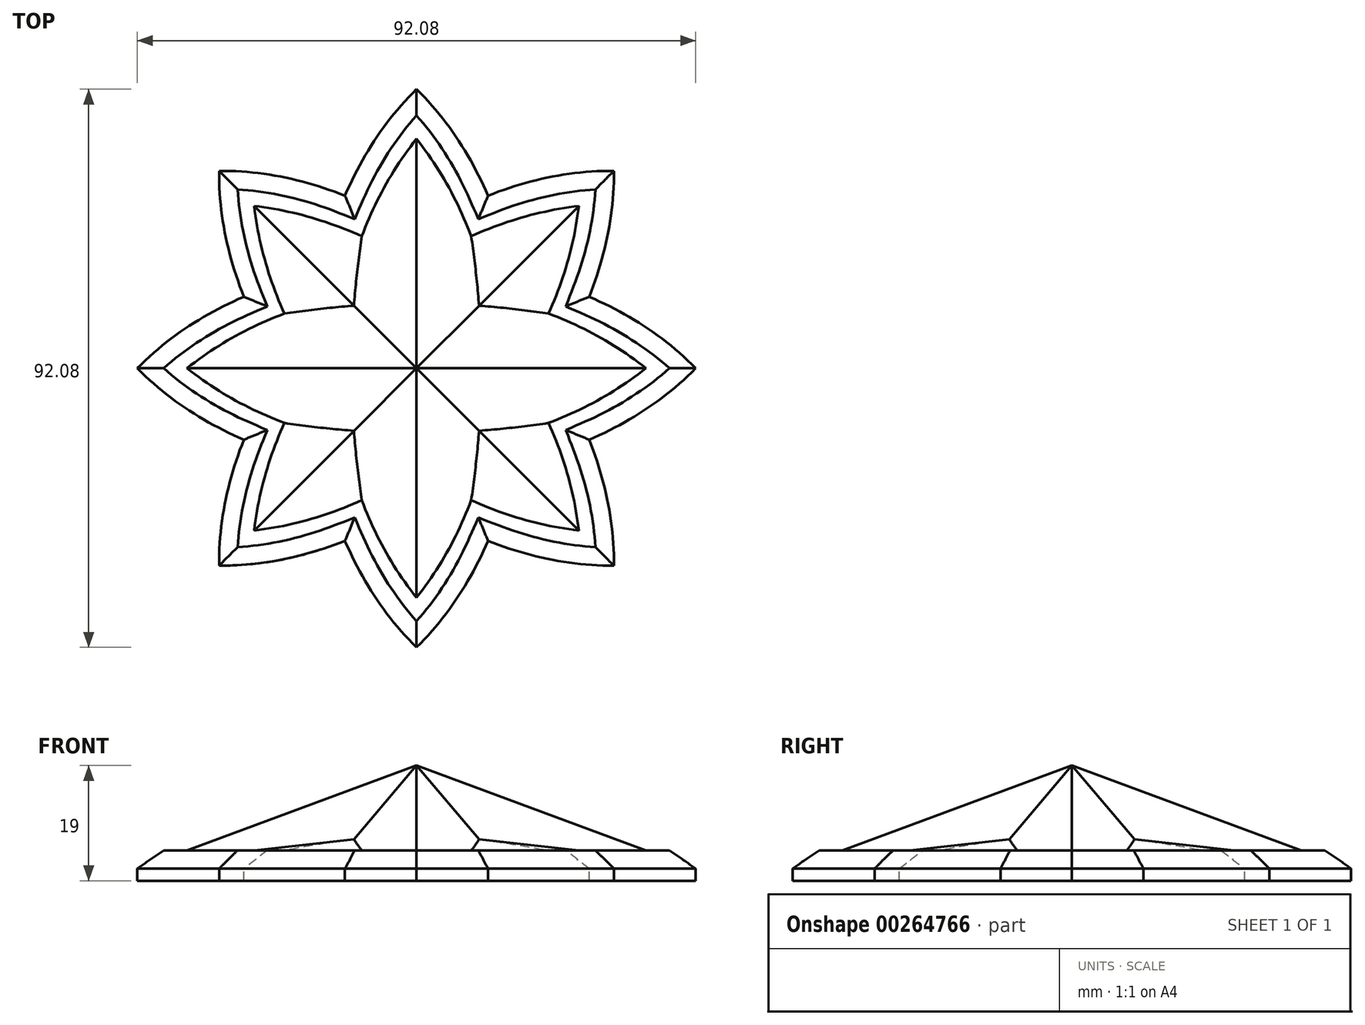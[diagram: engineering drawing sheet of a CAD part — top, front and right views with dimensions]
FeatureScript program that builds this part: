
annotation { "Feature Type Name" : "Feature", "Feature Type Description" : "" }
export const myFeature = defineFeature(function(context is Context, id is Id, definition is map)
    precondition{}
    {
        {
            var Q0;
            Q0=qCreatedBy(makeId("Top.planeOp"),FACE);
            var sketch = newSketch(context, id + "F0", { "sketchPlane" : qUnion([Q0])});
            skLineSegment(sketch, "E0", {"start": v(0, 45.34) * mm, "end": v(0, -44.66) * mm, "construction": true});
            skSolve(sketch);
        }
        {
            var Q0;
            Q0=qCreatedBy(makeId("Top.planeOp"),FACE);
            var sketch = newSketch(context, id + "F1", { "sketchPlane" : qUnion([Q0])});
            skFitSpline(sketch, "E1", {"points": [v(-11.88, 11.88) * mm, v(0, 37.85) * mm], "startDerivative": vector(5.9, 28.28) * mm, "endDerivative": vector(18.18, 22.98) * mm});
            skLineSegment(sketch, "E2", {"start": v(-11.88, 11.88) * mm, "end": v(0, 0) * mm, "construction": true});
            skFitSpline(sketch, "E3.MirrorCS", {"points": [v(11.88, 11.88) * mm, v(0, 37.85) * mm], "startDerivative": vector(-5.9, 28.28) * mm, "endDerivative": vector(-18.18, 22.98) * mm});
            skLineSegment(sketch, "E4.MirrorCS", {"start": v(11.88, 11.88) * mm, "end": v(0, 0) * mm, "construction": true});
            skFitSpline(sketch, "E5.MirrorCS", {"points": [v(-11.88, -11.88) * mm, v(-37.85, 0) * mm], "startDerivative": vector(-28.28, 5.9) * mm, "endDerivative": vector(-22.98, 18.18) * mm});
            skFitSpline(sketch, "E6.MirrorCS", {"points": [v(-11.88, 11.88) * mm, v(-37.85, 0) * mm], "startDerivative": vector(-28.28, -5.9) * mm, "endDerivative": vector(-22.98, -18.18) * mm});
            skFitSpline(sketch, "E7.MirrorCS", {"points": [v(11.88, 11.88) * mm, v(37.85, 0) * mm], "startDerivative": vector(28.28, -5.9) * mm, "endDerivative": vector(22.98, -18.18) * mm});
            skFitSpline(sketch, "E8.MirrorCS", {"points": [v(11.88, -11.88) * mm, v(37.85, 0) * mm], "startDerivative": vector(28.28, 5.9) * mm, "endDerivative": vector(22.98, 18.18) * mm});
            skFitSpline(sketch, "E9.MirrorCS", {"points": [v(11.88, -11.88) * mm, v(0, -37.85) * mm], "startDerivative": vector(-5.9, -28.28) * mm, "endDerivative": vector(-18.18, -22.98) * mm});
            skFitSpline(sketch, "E10.MirrorCS", {"points": [v(-11.88, -11.88) * mm, v(0, -37.85) * mm], "startDerivative": vector(5.9, -28.28) * mm, "endDerivative": vector(18.18, -22.98) * mm});
            skFitSpline(sketch, "E11", {"points": [v(-9.2, 21.3) * mm, v(-26, 26) * mm], "startDerivative": vector(-15.62, 6.86) * mm, "endDerivative": vector(-19.3, 2.67) * mm});
            skLineSegment(sketch, "E12", {"start": v(-26, 26) * mm, "end": v(0, 0) * mm, "construction": true});
            skFitSpline(sketch, "E13.MirrorCS", {"points": [v(9.2, 21.3) * mm, v(26, 26) * mm], "startDerivative": vector(15.62, 6.86) * mm, "endDerivative": vector(19.3, 2.67) * mm});
            skLineSegment(sketch, "E14.MirrorCS", {"start": v(26, 26) * mm, "end": v(0, 0) * mm, "construction": true});
            skFitSpline(sketch, "E15.MirrorCS", {"points": [v(-21.3, 9.2) * mm, v(-26, 26) * mm], "startDerivative": vector(-6.86, 15.62) * mm, "endDerivative": vector(-2.67, 19.3) * mm});
            skFitSpline(sketch, "E16.MirrorCS", {"points": [v(-21.3, -9.2) * mm, v(-26, -26) * mm], "startDerivative": vector(-6.86, -15.62) * mm, "endDerivative": vector(-2.67, -19.3) * mm});
            skFitSpline(sketch, "E17.MirrorCS", {"points": [v(21.3, 9.2) * mm, v(26, 26) * mm], "startDerivative": vector(6.86, 15.62) * mm, "endDerivative": vector(2.67, 19.3) * mm});
            skFitSpline(sketch, "E18.MirrorCS", {"points": [v(21.3, -9.2) * mm, v(26, -26) * mm], "startDerivative": vector(6.86, -15.62) * mm, "endDerivative": vector(2.67, -19.3) * mm});
            skFitSpline(sketch, "E19.MirrorCS", {"points": [v(9.2, -21.3) * mm, v(26, -26) * mm], "startDerivative": vector(15.62, -6.86) * mm, "endDerivative": vector(19.3, -2.67) * mm});
            skFitSpline(sketch, "E20.MirrorCS", {"points": [v(-9.2, -21.3) * mm, v(-26, -26) * mm], "startDerivative": vector(-15.62, -6.86) * mm, "endDerivative": vector(-19.3, -2.67) * mm});
            skSolve(sketch);
        }
        {
            var Q0;
            Q0=qCreatedBy(makeId("Top.planeOp"),FACE);
            cPlane(context, id + "F2", {"entities" : qUnion([Q0]), "cplaneType" : CPlaneType.OFFSET, "offset" : 14 * mm, "width" : 150 * mm, "height" : 150 * mm});
        }
        {
            var Q0;
            Q0=qCreatedBy(id+"F2.planeOp",FACE);
            var sketch = newSketch(context, id + "F3", { "sketchPlane" : qUnion([Q0])});
            skPoint(sketch, "E21", {"position": v(0, 0) * mm});
            skPoint(sketch, "E22", {"position": v(-11.88, -11.88) * mm});
            skPoint(sketch, "E23.MirrorP", {"position": v(11.88, -11.88) * mm});
            skPoint(sketch, "E24.MirrorP", {"position": v(-11.88, 11.88) * mm});
            skPoint(sketch, "E25.MirrorP", {"position": v(11.88, 11.88) * mm});
            skSolve(sketch);
        }
        {
            var Q0;
            {var subQ6=sQuery(id+"F1.wireOp",EDGE,"E6.MirrorCS");var subQ10=sQuery(id+"F1.wireOp",EDGE,"E1");var subQ11=makeQuery(id+"F1.imprint","INTERSECT",VERTEX,{"derivedFrom":[subQ10,subQ6]});Q0=makeQuery(id+"F1.imprint","IMPRINT",FACE,{"disambiguationData":[TD([[makeQuery(id+"F1.imprint","IMPRINT",EDGE,{"disambiguationData":[TD([[subQ11,-1.0]])],"derivedFrom":subQ10}),-1.0]])]});}
            var Q1;
            Q1=sQuery(id+"F3.wireOp",VERTEX,"E21");
            loft(context, id + "F4", {"sheetProfilesArray" : [{ "sheetProfileEntities" : qUnion([Q0]) }, { "sheetProfileEntities" : qUnion([Q1]) }]});
        }
        {
            var Q0;
            Q0=qCreatedBy(makeId("Top.planeOp"),FACE);
            cPlane(context, id + "F5", {"entities" : qUnion([Q0]), "cplaneType" : CPlaneType.OFFSET, "offset" : 3 * mm, "width" : 150 * mm, "height" : 150 * mm});
        }
        {
            var Q0;
            Q0=qCreatedBy(id+"F5.planeOp",FACE);
            var sketch = newSketch(context, id + "F6", { "sketchPlane" : qUnion([Q0])});
            skPoint(sketch, "E26", {"position": v(0, 0) * mm});
            skPoint(sketch, "E27", {"position": v(-11.88, -11.88) * mm});
            skPoint(sketch, "E28.MirrorP", {"position": v(11.88, -11.88) * mm});
            skPoint(sketch, "E29.MirrorP", {"position": v(-11.88, 11.88) * mm});
            skPoint(sketch, "E30.MirrorP", {"position": v(11.88, 11.88) * mm});
            skSolve(sketch);
        }
        {
            var Q0;
            Q0=qCreatedBy(makeId("Top.planeOp"),FACE);
            var sketch = newSketch(context, id + "F7", { "sketchPlane" : qUnion([Q0])});
            skFitSpline(sketch, "E31", {"points": [v(0, 16.8) * mm, v(26.76, 26.76) * mm], "startDerivative": vector(24.17, 15.83) * mm, "endDerivative": vector(29.1, 3.4) * mm});
            skFitSpline(sketch, "E32.MirrorCS", {"points": [v(16.8, 0) * mm, v(26.76, 26.76) * mm], "startDerivative": vector(15.83, 24.17) * mm, "endDerivative": vector(3.4, 29.1) * mm});
            skFitSpline(sketch, "E33.MirrorCS", {"points": [v(-16.8, 0) * mm, v(-26.76, 26.76) * mm], "startDerivative": vector(-15.83, 24.17) * mm, "endDerivative": vector(-3.4, 29.1) * mm});
            skFitSpline(sketch, "E34.MirrorCS", {"points": [v(0, 16.8) * mm, v(-26.76, 26.76) * mm], "startDerivative": vector(-24.17, 15.83) * mm, "endDerivative": vector(-29.1, 3.4) * mm});
            skFitSpline(sketch, "E35.MirrorCS", {"points": [v(16.8, 0) * mm, v(26.76, -26.76) * mm], "startDerivative": vector(15.83, -24.17) * mm, "endDerivative": vector(3.4, -29.1) * mm});
            skFitSpline(sketch, "E36.MirrorCS", {"points": [v(0, -16.8) * mm, v(26.76, -26.76) * mm], "startDerivative": vector(24.17, -15.83) * mm, "endDerivative": vector(29.1, -3.4) * mm});
            skFitSpline(sketch, "E37.MirrorCS", {"points": [v(0, -16.8) * mm, v(-26.76, -26.76) * mm], "startDerivative": vector(-24.17, -15.83) * mm, "endDerivative": vector(-29.1, -3.4) * mm});
            skFitSpline(sketch, "E38.MirrorCS", {"points": [v(-16.8, 0) * mm, v(-26.76, -26.76) * mm], "startDerivative": vector(-15.83, -24.17) * mm, "endDerivative": vector(-3.4, -29.1) * mm});
            skSolve(sketch);
        }
        {
            var Q0;
            Q0=makeQuery(id+"F7.imprint","IMPRINT",FACE,{"disambiguationData":[TD([[makeQuery(id+"F7.imprint","IMPRINT",EDGE,{"derivedFrom":sQuery(id+"F7.wireOp",EDGE,"E31")}),-1.0]])]});
            var Q1;
            Q1=sQuery(id+"F6.wireOp",VERTEX,"E26");
            loft(context, id + "F8", {"operationType" : NewBodyOperationType.ADD, "sheetProfilesArray" : [{ "sheetProfileEntities" : qUnion([Q0]) }, { "sheetProfileEntities" : qUnion([Q1]) }]});
        }
        {
            var Q0;
            Q0=qCreatedBy(makeId("Top.planeOp"),FACE);
            var sketch = newSketch(context, id + "F9", { "sketchPlane" : qUnion([Q0])});
            skFitSpline(sketch, "E39", {"points": [v(-11.8, 28.47) * mm, v(0, 46.04) * mm], "startDerivative": vector(8.54, 19.71) * mm, "endDerivative": vector(15.3, 14.96) * mm});
            skLineSegment(sketch, "E40", {"start": v(-11.8, 28.47) * mm, "end": v(0, 0) * mm, "construction": true});
            skFitSpline(sketch, "E41.MirrorCS", {"points": [v(11.8, 28.47) * mm, v(0, 46.04) * mm], "startDerivative": vector(-8.54, 19.71) * mm, "endDerivative": vector(-15.3, 14.96) * mm});
            skLineSegment(sketch, "E42.MirrorCS", {"start": v(11.8, 28.47) * mm, "end": v(0, 0) * mm, "construction": true});
            skFitSpline(sketch, "E43.MirrorCS", {"points": [v(-28.47, 11.8) * mm, v(-32.55, 32.55) * mm], "startDerivative": vector(-7.9, 19.98) * mm, "endDerivative": vector(0.23, 21.4) * mm});
            skFitSpline(sketch, "E44.MirrorCS", {"points": [v(-11.8, 28.47) * mm, v(-32.55, 32.55) * mm], "startDerivative": vector(-19.98, 7.9) * mm, "endDerivative": vector(-21.4, -0.23) * mm});
            skFitSpline(sketch, "E45.MirrorCS", {"points": [v(11.8, 28.47) * mm, v(32.55, 32.55) * mm], "startDerivative": vector(19.98, 7.9) * mm, "endDerivative": vector(21.4, -0.23) * mm});
            skFitSpline(sketch, "E46.MirrorCS", {"points": [v(28.47, 11.8) * mm, v(32.55, 32.55) * mm], "startDerivative": vector(7.9, 19.98) * mm, "endDerivative": vector(-0.23, 21.4) * mm});
            skFitSpline(sketch, "E47.MirrorCS", {"points": [v(28.47, 11.8) * mm, v(46.04, 0) * mm], "startDerivative": vector(19.71, -8.54) * mm, "endDerivative": vector(14.96, -15.3) * mm});
            skFitSpline(sketch, "E48.MirrorCS", {"points": [v(28.47, -11.8) * mm, v(46.04, 0) * mm], "startDerivative": vector(19.71, 8.54) * mm, "endDerivative": vector(14.96, 15.3) * mm});
            skFitSpline(sketch, "E49.MirrorCS", {"points": [v(-28.47, 11.8) * mm, v(-46.04, 0) * mm], "startDerivative": vector(-19.71, -8.54) * mm, "endDerivative": vector(-14.96, -15.3) * mm});
            skFitSpline(sketch, "E50.MirrorCS", {"points": [v(-28.47, -11.8) * mm, v(-46.04, 0) * mm], "startDerivative": vector(-19.71, 8.54) * mm, "endDerivative": vector(-14.96, 15.3) * mm});
            skFitSpline(sketch, "E51.MirrorCS", {"points": [v(-28.47, -11.8) * mm, v(-32.55, -32.55) * mm], "startDerivative": vector(-7.9, -19.98) * mm, "endDerivative": vector(0.23, -21.4) * mm});
            skFitSpline(sketch, "E52.MirrorCS", {"points": [v(-11.8, -28.47) * mm, v(-32.55, -32.55) * mm], "startDerivative": vector(-19.98, -7.9) * mm, "endDerivative": vector(-21.4, 0.23) * mm});
            skFitSpline(sketch, "E53.MirrorCS", {"points": [v(-11.8, -28.47) * mm, v(0, -46.04) * mm], "startDerivative": vector(8.54, -19.71) * mm, "endDerivative": vector(15.3, -14.96) * mm});
            skFitSpline(sketch, "E54.MirrorCS", {"points": [v(11.8, -28.47) * mm, v(0, -46.04) * mm], "startDerivative": vector(-8.54, -19.71) * mm, "endDerivative": vector(-15.3, -14.96) * mm});
            skFitSpline(sketch, "E55.MirrorCS", {"points": [v(11.8, -28.47) * mm, v(32.55, -32.55) * mm], "startDerivative": vector(19.98, -7.9) * mm, "endDerivative": vector(21.4, 0.23) * mm});
            skFitSpline(sketch, "E56.MirrorCS", {"points": [v(28.47, -11.8) * mm, v(32.55, -32.55) * mm], "startDerivative": vector(7.9, -19.98) * mm, "endDerivative": vector(-0.23, -21.4) * mm});
            skSolve(sketch);
        }
        {
            var Q0;
            Q0=makeQuery(id+"F9.imprint","IMPRINT",FACE,{"disambiguationData":[TD([[makeQuery(id+"F9.imprint","IMPRINT",EDGE,{"derivedFrom":sQuery(id+"F9.wireOp",EDGE,"E39")}),-1.0]])]});
            extrude(context, id + "F10", {"entities" : qUnion([Q0]), "operationType" : NewBodyOperationType.ADD, "oppositeDirection" : true, "depth" : 5 * mm, "offsetDistance" : 25 * mm});
        }
        {
            var Q0;
            Q0=makeQuery(id+"F10.opExtrude","CAP_EDGE",EDGE,{"disambiguationData":[OSD([sQuery(id+"F9.wireOp",EDGE,"E54.MirrorCS")])],"isStart":true});
            var Q1;
            Q1=makeQuery(id+"F10.opExtrude","CAP_EDGE",EDGE,{"disambiguationData":[OSD([sQuery(id+"F9.wireOp",EDGE,"E55.MirrorCS")])],"isStart":true});
            var Q2;
            Q2=makeQuery(id+"F10.opExtrude","CAP_EDGE",EDGE,{"disambiguationData":[OSD([sQuery(id+"F9.wireOp",EDGE,"E56.MirrorCS")])],"isStart":true});
            var Q3;
            Q3=makeQuery(id+"F10.opExtrude","CAP_EDGE",EDGE,{"disambiguationData":[OSD([sQuery(id+"F9.wireOp",EDGE,"E48.MirrorCS")])],"isStart":true});
            var Q4;
            Q4=makeQuery(id+"F10.opExtrude","CAP_EDGE",EDGE,{"disambiguationData":[OSD([sQuery(id+"F9.wireOp",EDGE,"E53.MirrorCS")])],"isStart":true});
            var Q5;
            Q5=makeQuery(id+"F10.opExtrude","CAP_EDGE",EDGE,{"disambiguationData":[OSD([sQuery(id+"F9.wireOp",EDGE,"E52.MirrorCS")])],"isStart":true});
            var Q6;
            Q6=makeQuery(id+"F10.opExtrude","CAP_EDGE",EDGE,{"disambiguationData":[OSD([sQuery(id+"F9.wireOp",EDGE,"E51.MirrorCS")])],"isStart":true});
            var Q7;
            Q7=makeQuery(id+"F10.opExtrude","CAP_EDGE",EDGE,{"disambiguationData":[OSD([sQuery(id+"F9.wireOp",EDGE,"E47.MirrorCS")])],"isStart":true});
            var Q8;
            Q8=makeQuery(id+"F10.opExtrude","CAP_EDGE",EDGE,{"disambiguationData":[OSD([sQuery(id+"F9.wireOp",EDGE,"E46.MirrorCS")])],"isStart":true});
            var Q9;
            Q9=makeQuery(id+"F10.opExtrude","CAP_EDGE",EDGE,{"disambiguationData":[OSD([sQuery(id+"F9.wireOp",EDGE,"E45.MirrorCS")])],"isStart":true});
            var Q10;
            Q10=makeQuery(id+"F10.opExtrude","CAP_EDGE",EDGE,{"disambiguationData":[OSD([sQuery(id+"F9.wireOp",EDGE,"E41.MirrorCS")])],"isStart":true});
            var Q11;
            Q11=makeQuery(id+"F10.opExtrude","CAP_EDGE",EDGE,{"disambiguationData":[OSD([sQuery(id+"F9.wireOp",EDGE,"E39")])],"isStart":true});
            var Q12;
            Q12=makeQuery(id+"F10.opExtrude","CAP_EDGE",EDGE,{"disambiguationData":[OSD([sQuery(id+"F9.wireOp",EDGE,"E44.MirrorCS")])],"isStart":true});
            var Q13;
            Q13=makeQuery(id+"F10.opExtrude","CAP_EDGE",EDGE,{"disambiguationData":[OSD([sQuery(id+"F9.wireOp",EDGE,"E43.MirrorCS")])],"isStart":true});
            var Q14;
            Q14=makeQuery(id+"F10.opExtrude","CAP_EDGE",EDGE,{"disambiguationData":[OSD([sQuery(id+"F9.wireOp",EDGE,"E49.MirrorCS")])],"isStart":true});
            var Q15;
            Q15=makeQuery(id+"F10.opExtrude","CAP_EDGE",EDGE,{"disambiguationData":[OSD([sQuery(id+"F9.wireOp",EDGE,"E50.MirrorCS")])],"isStart":true});
            chamfer(context, id + "F11", {"entities" : qUnion([Q0, Q1, Q2, Q3, Q4, Q5, Q6, Q7, Q8, Q9, Q10, Q11, Q12, Q13, Q14, Q15]), "width" : 3 * mm, "tangentPropagation" : true});
        }
    });
